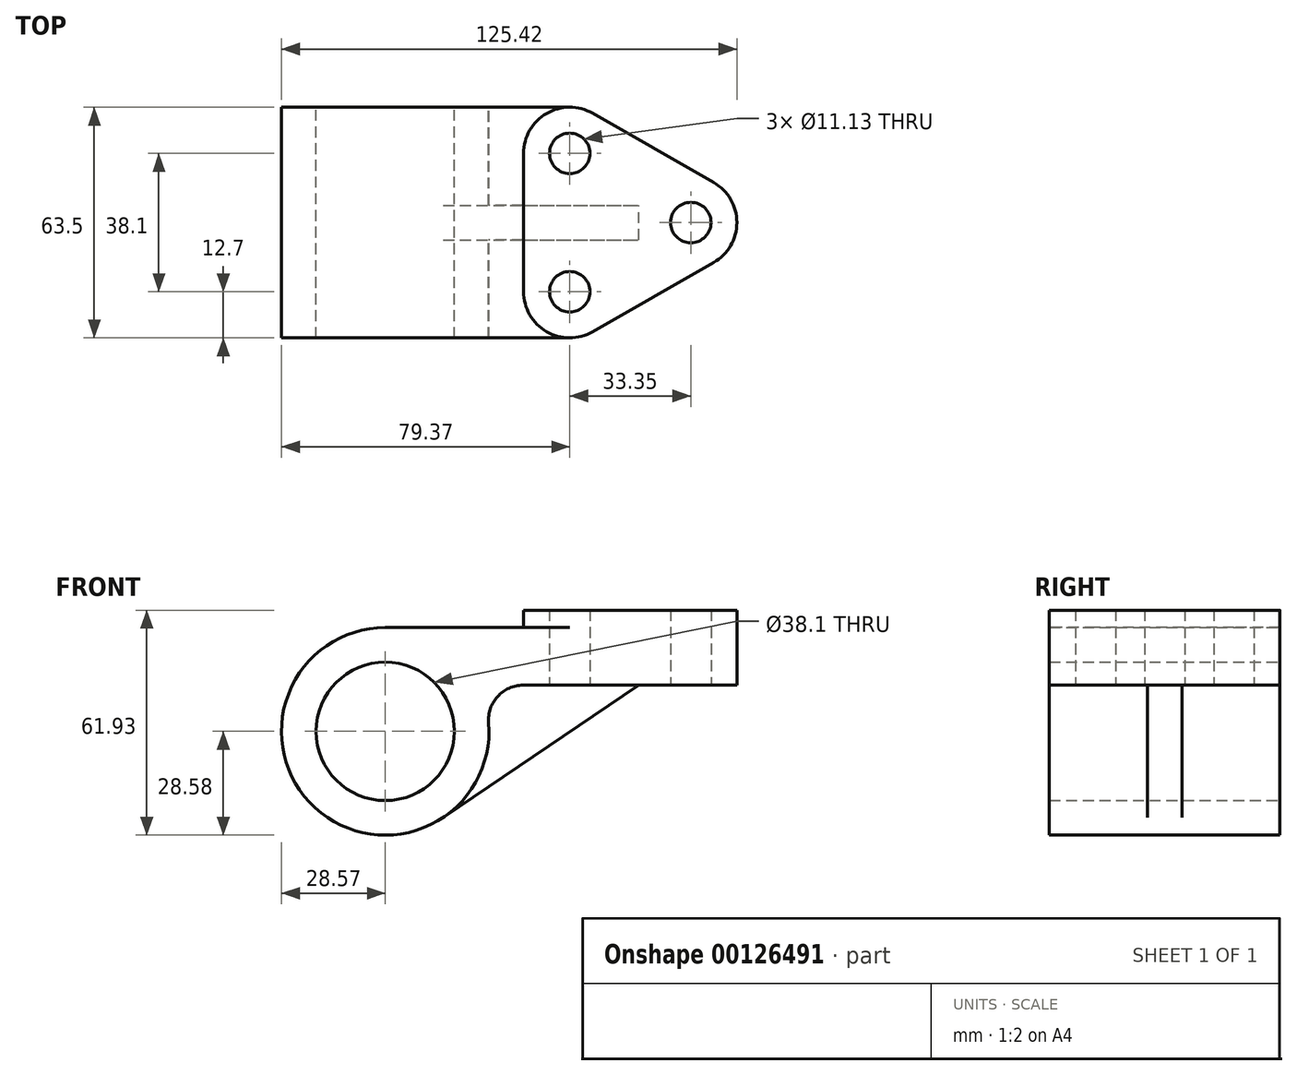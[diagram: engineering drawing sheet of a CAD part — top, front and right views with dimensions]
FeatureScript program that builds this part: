
annotation { "Feature Type Name" : "Feature", "Feature Type Description" : "" }
export const myFeature = defineFeature(function(context is Context, id is Id, definition is map)
    precondition{}
    {
        {
            var Q0;
            Q0=qCreatedBy(makeId("Front.planeOp"),FACE);
            var sketch = newSketch(context, id + "F0", { "sketchPlane" : qUnion([Q0])});
            skCircle(sketch, "E0", {"center": v(0, 0) * mm, "radius": 19.05 * mm});
            skLineSegment(sketch, "E1", {"start": v(0, 28.58) * mm, "end": v(50.8, 28.58) * mm});
            skLineSegment(sketch, "E2", {"start": v(50.8, 28.58) * mm, "end": v(50.8, 12.7) * mm});
            skArc(sketch, "E3", {"start": v(0, 28.58) * mm, "mid": v(-19.35, -21.03) * mm, "end": v(28.48, 2.38) * mm});
            skLineSegment(sketch, "E4", {"start": v(37.97, 12.7) * mm, "end": v(50.8, 12.7) * mm});
            skPoint(sketch, "E5.visualSharp", {"position": v(25.6, 12.7) * mm});
            skArc(sketch, "E5.filletArc", {"start": v(37.97, 12.7) * mm, "mid": v(30.96, 9.62) * mm, "end": v(28.48, 2.38) * mm});
            skSolve(sketch);
        }
        {
            var Q0;
            Q0=qSketchRegion(id+"F0",true);
            extrude(context, id + "F1", {"entities" : qUnion([Q0]), "endBound" : BoundingType.SYMMETRIC, "depth" : 63.5 * mm});
        }
        {
            var Q0;
            Q0=makeQuery(id+"F1.opExtrude","SWEPT_FACE",FACE,{"disambiguationData":[OSD([sQuery(id+"F0.wireOp",EDGE,"E4")])]});
            var sketch = newSketch(context, id + "F2", { "sketchPlane" : qUnion([Q0])});
            skLineSegment(sketch, "E6", {"start": v(38.1, 19.05) * mm, "end": v(38.1, -19.05) * mm});
            skLineSegment(sketch, "E7", {"start": v(57.1, 30.08) * mm, "end": v(90.45, 11.03) * mm});
            skLineSegment(sketch, "E8", {"start": v(57.1, -30.08) * mm, "end": v(90.45, -11.03) * mm});
            skArc(sketch, "E9", {"start": v(90.45, -11.03) * mm, "mid": v(96.85, 0) * mm, "end": v(90.45, 11.03) * mm});
            skArc(sketch, "E10", {"start": v(57.1, 30.08) * mm, "mid": v(44.42, 30.03) * mm, "end": v(38.1, 19.05) * mm});
            skArc(sketch, "E11", {"start": v(38.1, -19.05) * mm, "mid": v(44.42, -30.03) * mm, "end": v(57.1, -30.08) * mm});
            skCircle(sketch, "E12", {"center": v(50.8, 19.05) * mm, "radius": 5.56 * mm});
            skCircle(sketch, "E13", {"center": v(50.8, -19.05) * mm, "radius": 5.56 * mm});
            skCircle(sketch, "E14", {"center": v(84.15, 0) * mm, "radius": 5.56 * mm});
            skLineSegment(sketch, "E15", {"start": v(0, 0) * mm, "end": v(84.15, 0) * mm, "construction": true});
            skSolve(sketch);
        }
        {
            var Q0;
            {var subQ12=sQuery(id+"F2.wireOp",EDGE,"E7");Q0=makeQuery(id+"F2.imprint","IMPRINT",FACE,{"disambiguationData":[TD([[makeQuery(id+"F2.imprint","IMPRINT",EDGE,{"derivedFrom":subQ12}),-1.0]])]});}
            var Q1;
            {var subQ4=sQuery(id+"F2.wireOp",EDGE,"E6");Q1=makeQuery(id+"F2.imprint","IMPRINT",FACE,{"disambiguationData":[TD([[makeQuery(id+"F2.imprint","IMPRINT",EDGE,{"derivedFrom":subQ4}),1.0]])]});}
            extrude(context, id + "F3", {"entities" : qUnion([Q0, Q1]), "operationType" : NewBodyOperationType.ADD, "oppositeDirection" : true, "depth" : 20.65 * mm});
        }
        {
            var Q0;
            Q0=makeQuery(id+"F3.boolean.opBoolean","SPLIT",FACE,{"disambiguationData":[TD([makeQuery(id+"F3.opExtrude","SWEPT_FACE",FACE,{"disambiguationData":[OSD([sQuery(id+"F2.wireOp",EDGE,"E13")])]})])],"derivedFrom":makeQuery(id+"F1.opExtrude","SWEPT_FACE",FACE,{"disambiguationData":[OSD([sQuery(id+"F0.wireOp",EDGE,"E1")])]})});
            var Q1;
            Q1=makeQuery(id+"F3.boolean.opBoolean","SPLIT",FACE,{"disambiguationData":[TD([makeQuery(id+"F3.opExtrude","SWEPT_FACE",FACE,{"disambiguationData":[OSD([sQuery(id+"F2.wireOp",EDGE,"E12")])]})])],"derivedFrom":makeQuery(id+"F1.opExtrude","SWEPT_FACE",FACE,{"disambiguationData":[OSD([sQuery(id+"F0.wireOp",EDGE,"E1")])]})});
            extrude(context, id + "F4", {"entities" : qUnion([Q0, Q1]), "operationType" : NewBodyOperationType.REMOVE, "endBound" : BoundingType.THROUGH_ALL, "oppositeDirection" : true, "depth" : 25.4 * mm});
        }
        {
            var Q0;
            Q0=qCreatedBy(makeId("Front.planeOp"),FACE);
            var sketch = newSketch(context, id + "F5", { "sketchPlane" : qUnion([Q0])});
            skLineSegment(sketch, "E16", {"start": v(16, -23.68) * mm, "end": v(69.85, 12.7) * mm});
            skArc(sketch, "E17.0", {"start": v(16, -23.68) * mm, "mid": v(25.77, -12.34) * mm, "end": v(28.48, 2.38) * mm});
            skArc(sketch, "E18.0", {"start": v(37.97, 12.7) * mm, "mid": v(30.96, 9.62) * mm, "end": v(28.48, 2.38) * mm});
            skLineSegment(sketch, "E19.0", {"start": v(37.97, 12.7) * mm, "end": v(50.8, 12.7) * mm});
            skLineSegment(sketch, "E20.0", {"start": v(57.1, 12.7) * mm, "end": v(50.8, 12.7) * mm});
            skLineSegment(sketch, "E21.0", {"start": v(57.1, 12.7) * mm, "end": v(69.85, 12.7) * mm});
            skPoint(sketch, "E22.orphan", {"position": v(0, 28.58) * mm});
            skPoint(sketch, "E23.orphan", {"position": v(90.45, 12.7) * mm});
            skSolve(sketch);
        }
        {
            var Q0;
            Q0=makeQuery(id+"F5.imprint","IMPRINT",FACE,{"disambiguationData":[TD([[makeQuery(id+"F5.imprint","IMPRINT",EDGE,{"derivedFrom":sQuery(id+"F5.wireOp",EDGE,"E16")}),1.0]])]});
            extrude(context, id + "F6", {"entities" : qUnion([Q0]), "operationType" : NewBodyOperationType.ADD, "endBound" : BoundingType.SYMMETRIC, "depth" : 9.52 * mm});
        }
    });
